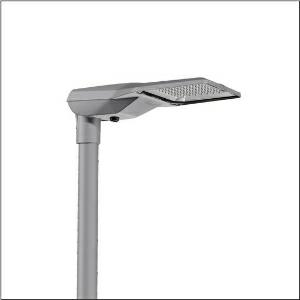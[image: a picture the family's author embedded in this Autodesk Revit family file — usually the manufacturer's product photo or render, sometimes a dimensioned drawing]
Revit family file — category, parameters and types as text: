
# Revit family: streetlight_sl_21_midi___p0_8a_5xe3u33r08mb_4c8c
name_source: partatom
category: Lighting Fixtures
units: mm (PartAtom-declared; Revit-internal decimal feet)

## family parameters
Cut with Voids When Loaded = No
Host = Face
Light Source = No
Part Type = Normal
Room Calculation Point = No
Round Connector Dimension = Use Diameter
Shared = No

## types (1)
- --- (1 x LED, 18430 lm, 136 W, 3000K)
    Apparent Load = 136 VA
    CIE Flux Codes = 33 69 96 100 100
    Color Rendering = 70
    Color Temperature = 3000K
    Default Elevation = 1800 mm
    Description = Streetlight SL 21 midi, mast luminaire, primary light control with lens, of PMMA, primary optical cover: cover, of toughened safety glass, transparent, light distribution: P0.8a, light emission: direct distribution, primary light characteristic: asymmetric, installation type: post-top, side-entry, LED, High Power LED, rated luminous flux: 18.430lm, luminous efficacy: 136lm/W, light colour: 730, colour temperature: 3000K, control gear: D4i, control: pre-setting: logarithmic dimming characteristic, flexible luminous flux parameterisation, time-dependent luminous flux control, constant luminous flux control, overheat protection, mains connection: 230..240V, AC, 50/60Hz, start of lifetime: 136W, end of service life: 142W, reduction: 61W, luminaire housing, of diecast aluminium, powder-coated, Siteco® metallic grey (DB 702S), corrosivity category C5 mid according to DIN EN ISO 12944, multi-level sealing system, sealing non-destructively replaceable, inclination adjustable: 0°, 5°, 10°, 15°, please order mast flange separately, length: 644mm, width: 335mm, height: 110mm, mast flange for spigot size: 42mm (side-entry): 5XC10008XM4, 60/48mm (side-entry/post-top): 5XC10108XM2, 76/60mm (side-entry/post-top): 5XC10108XM1, mounting height: 4..8m, Smart Interface below, protection rating (complete): IP66, insulation class (complete): insulation class II (safety insulation), certification: CE, ENEC, ENEC+, VDE, impact resistance: IK10, permissible operating ambient temperature for outdoor applications: -40..+50°C, standard-compliant lighting for roads and squares, packaging unit: 1 piece

Light Distribution: P0.8a
    Height = 111 mm
    Lamp = 1 x LED
    Lamp Light Flux = 18430 lm
    Lamp Power = 136 W
    Lamp count = 1
    Length = 644 mm
    Luminous efficacy = 136 lm/W
    Manufacturer = Siteco
    ModVariant = No
    Model = 5XE3U33R08MB
    Number of Poles = 1
    OnlyDefault = Yes
    Power Factor = 1
    Product Name = Streetlight SL 21 midi | P0.8a
    Product group = mast luminaire | pylon top
    ProductGroupID = 6100
    Protection Class = Protection class II
    Protection Degree = IP 66
    RLX_Detail_Level = 1
    RLX_Emergency_Light_Flux = 0 lm
    RLX_Emergency_Type = 0
    RLX_Emergency_Type_DB = No
    RlxData = <blob elided: 26721 chars, md5=e3d4711c>
    Socket = socket
    Standby Power = 0 W
    System Light Flux = 18429 lm
    System Power = 136 W
    Type Comments = factory setting: luminous flux: 100 % | dim-lin: 254 | 695 mA
    Type Image = l_1004300.jpg
    URL = http://relux.com
    VarID = @adj_072662
    Voltage = 0 V
    Weight = 0.00 kg
    Width = 336 mm

## geometry (parser evidence)
native form markers: Blend x4, Sweep x10
no freeform markers — native parametric forms only
